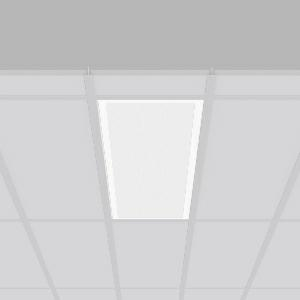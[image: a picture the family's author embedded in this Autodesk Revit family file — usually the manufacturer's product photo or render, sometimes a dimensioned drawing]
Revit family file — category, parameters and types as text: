
# Revit family: sidelite_eco_672373_002_1_89_3a14
name_source: partatom
category: Lighting Fixtures
units: mm (PartAtom-declared; Revit-internal decimal feet)

## family parameters
Cut with Voids When Loaded = No
Host = Face
Light Source = No
Part Type = Normal
Room Calculation Point = No
Round Connector Dimension = Use Diameter
Shared = No

## types (1)
- SIDELITE ECO (1 x LED Modul 840, 3500 lm, 4000)
    Apparent Load = 30 VA
    Approval mark = CE
    CIE Flux Codes = 59 87 97 100 100
    Color Rendering = 80
    Color Temperature = 4000
    Default Elevation = 1800 mm
    Description = Series: SIDELITE ECO
Highly economical recessed luminaire with progressive LED technology. For escape route illumination. Frame made of aluminium, powder-coated. Diffuser plastic microprismatic. Lightguide and diffuser made of non-yellowing plastic (PMMA). Lateral light emission (RZB SIDELITE technology) for homogeneous light distribution. External driver. Second cable inlet for loop through. With AC Control monitoring module for LUXIFAIR central battery units. External driver with simple plug-in locking system. Extended connection cable (1.90 m). 
Colour: white
Length: 1245 mm
Width: 308 mm
Cut-out length: 1220 mm
Cut-out width: 285 mm
Recess height: 160 mm
Luminaire: recess height: 40 mm
Weight: 4.19 kg
Operating mode: maintained power mode
Lamp: LED
Socket: without socket
Colour temperature: 4000K
Colour rendering index (CRI): 80
System power: 30 W
Rated luminous flux: 3500 lm
Luminous flux, emergency: 3500 lm
System power, emergency: 30 W
Control gear: Regulated power supply
Protection class: I
Type of protection: IP 20
    Height = 0 mm  [stored 0 ft]
    Lamp = 1 x LED Modul 840
    Lamp Light Flux = 3500 lm
    Lamp count = 1
    Length = 1245 mm
    Lifetime = 50000 h
    Luminous efficacy = 117 lm/W
    Manufacturer = RZB
    ModVariant = No
    Model = 672373.002.1.89
    Mounting Place = Ceiling
    Mounting Type = Recessed
    Number of Poles = 1
    OnlyDefault = Yes
    Power Factor = 1
    Product Name = SIDELITE ECO
    Product group = Recessed modular luminaires
    ProductGroupID = 406
    Protection Class = Protection class I
    Protection Degree = IP 20
    RLX_Detail_Level = 1
    RLX_Emergency_Light_Flux = 3500 lm
    RLX_Emergency_Type = 3
    RLX_Emergency_Type_DB = Yes
    RlxData = <blob elided: 34777 chars, md5=d5c5c2c1>
    Socket = socket
    Standby Power = 0 W
    System Light Flux = 3500 lm
    System Power = 30 W
    Type Comments = Product without accessories
    Type Image = 312368.002.jpg
    URL = http://relux.com
    VarID = ---
    Voltage = 230 V
    Voltage Range = 220-240 V
    Weight = 0.00 kg
    Width = 308 mm

note: [stored X ft] marks values corroborated as IEEE doubles in the binary element streams (Revit-internal decimal feet)

## geometry (parser evidence)
native form markers: Blend x4, Sweep x10
no freeform markers — native parametric forms only
